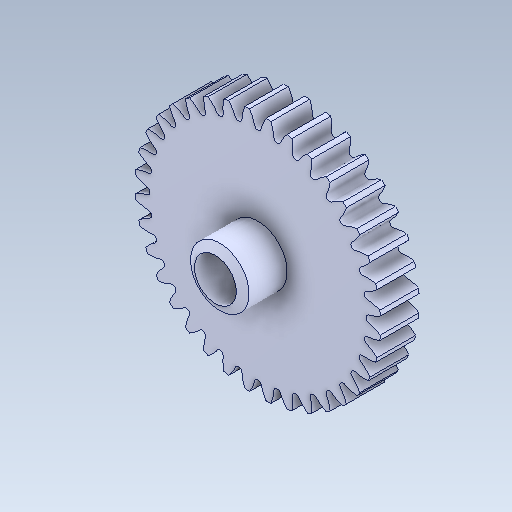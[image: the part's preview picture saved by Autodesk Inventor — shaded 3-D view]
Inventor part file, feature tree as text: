
AUTODESK INVENTOR PART (.ipt)
format: ipt  version: 2020 (Build 240168000, 168)  size: 397,312 bytes
history: native  units: in
note: dims shown in document units (in); Inventor stores cm internally (conversion verified against a paired STEP export)
features: chamfer x1
ambient origin geometry x8: Origin, YZ Plane, XZ Plane, XY Plane, X Axis, Y Axis, Z Axis, Center Point
bodies: Solid1 (feature_tree)
feature tree (1):
  chamfer  "Chamfer1"  [1 undecoded]
note: 1 required parameter value undecoded (feature->parameter linkage not recoverable at this tier; creation-order binding heuristic only, values carry confidence <= 0.55)
